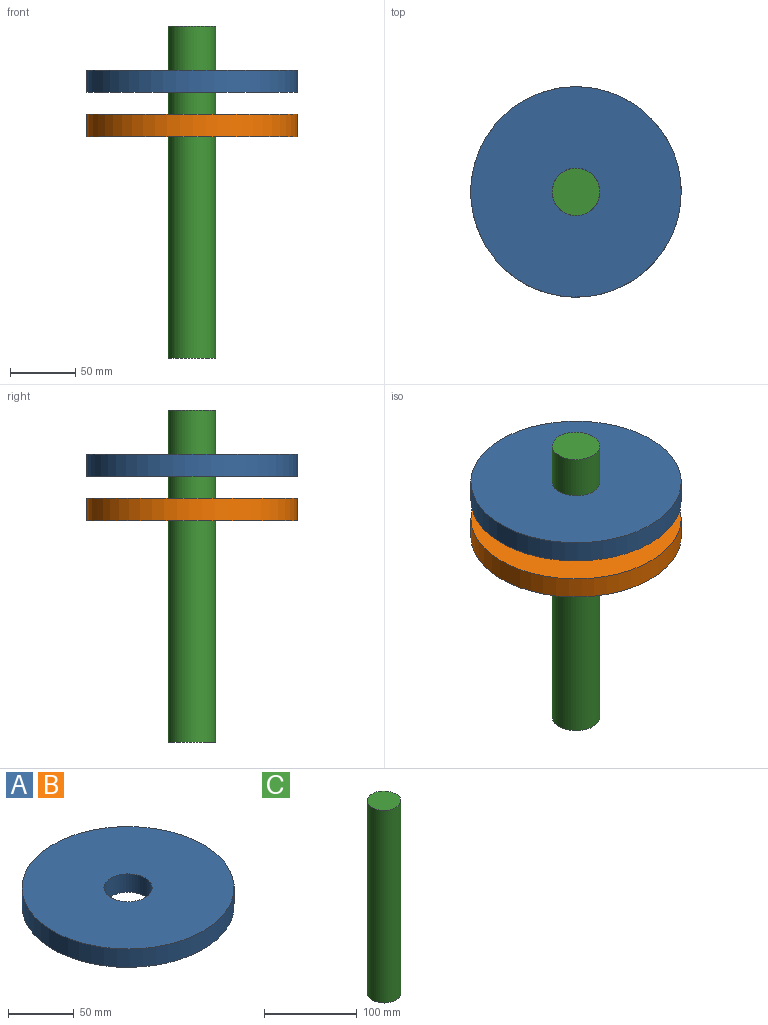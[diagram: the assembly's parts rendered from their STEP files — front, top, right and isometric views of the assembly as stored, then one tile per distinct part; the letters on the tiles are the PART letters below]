
ASSEMBLY  parts=3 mates=2
PART A: 4 faces, bbox 161x161x17 mm
  f0: cylinder r=80.49mm len=160.97mm, axis (0,0,-1), area 8606.2mm2, adj f1,f2
  f1: plane 160.97x160.97mm, normal (0,0,1), area 19303.5mm2, adj f0,f3
  f2: plane 160.97x160.97mm, normal (0,0,-1), area 19303.5mm2, adj f0,f3
  f3: cylinder r=18.26mm len=36.53mm, axis (0,0,-1), area 1953mm2, adj f1,f2
PART B: same geometry as A
PART C: 3 faces, bbox 36.3x36.3x254 mm
  f0: cylinder r=18.14mm len=254mm, axis (0,0,-1), area 28949.5mm2, adj f1,f2
  f1: plane 36.28x36.28mm, normal (0,0,1), area 1033.7mm2, adj f0
  f2: plane 36.28x36.28mm, normal (0,0,-1), area 1033.7mm2, adj f0
PLACE A t=(-234.72,-84.13,20.88)mm
PLACE B rot(axis=(0,0,1),136.3deg) t=(-234.72,-84.13,-13.03)mm
PLACE C t=(-234.72,-84.13,-55.32)mm fixed
MATE revolute C.f0 <-> A.f0  axis (0,0,1) through (-234.72,-84.13,71.68)mm
MATE revolute C.f0 <-> B.f0  axis (0,0,-1) through (-234.72,-84.13,-55.32)mm
